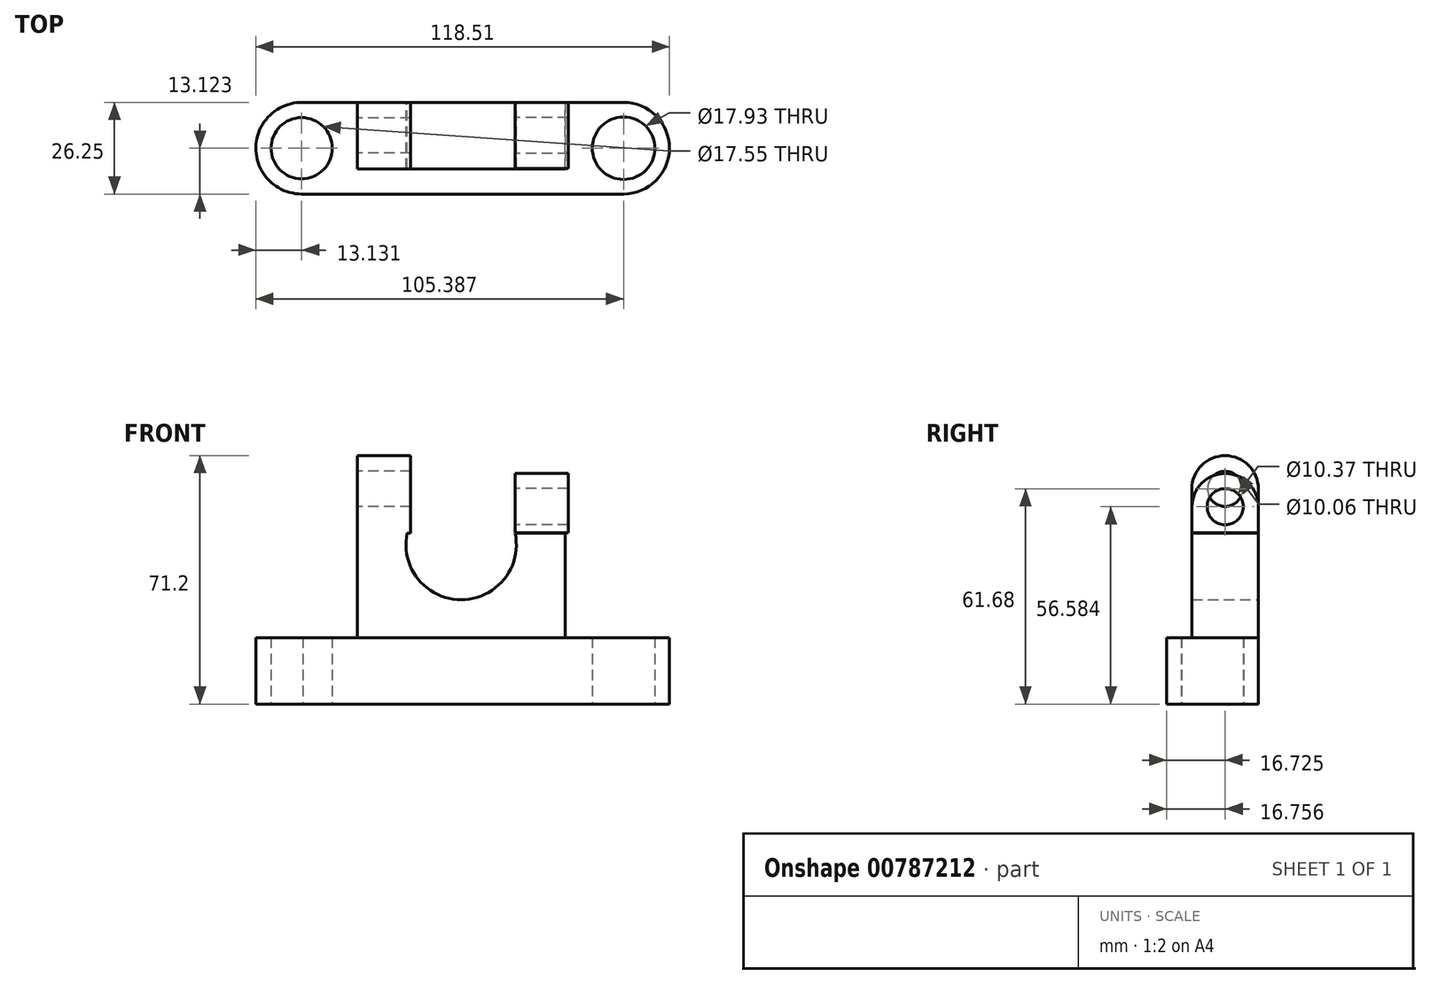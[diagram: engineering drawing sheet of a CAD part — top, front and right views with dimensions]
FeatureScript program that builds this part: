
annotation { "Feature Type Name" : "Feature", "Feature Type Description" : "" }
export const myFeature = defineFeature(function(context is Context, id is Id, definition is map)
    precondition{}
    {
        {
            var Q0;
            Q0=qCreatedBy(makeId("Top.planeOp"),FACE);
            var sketch = newSketch(context, id + "F0", { "sketchPlane" : qUnion([Q0])});
            skLineSegment(sketch, "E0.bottom", {"start": v(-60.85, 0) * mm, "end": v(31.08, 0) * mm});
            skLineSegment(sketch, "E1.bottom", {"start": v(-61.18, -26.25) * mm, "end": v(31.08, -26.25) * mm});
            skLineSegment(sketch, "E1.top", {"start": v(-61.18, 0) * mm, "end": v(31.08, 0) * mm});
            skCircle(sketch, "E2", {"center": v(-61.18, -13.13) * mm, "radius": 8.78 * mm});
            skCircle(sketch, "E3", {"center": v(31.08, -13.13) * mm, "radius": 8.96 * mm});
            skArc(sketch, "E4", {"start": v(-60.85, 0) * mm, "mid": v(-74.3, -12.96) * mm, "end": v(-61.18, -26.25) * mm});
            skArc(sketch, "E5", {"start": v(31.08, -26.25) * mm, "mid": v(44.2, -13.13) * mm, "end": v(31.08, 0) * mm});
            skSolve(sketch);
        }
        {
            var Q0;
            {var subQ4=sQuery(id+"F0.wireOp",EDGE,"E0.bottom");Q0=makeQuery(id+"F0.imprint","IMPRINT",FACE,{"disambiguationData":[TD([[makeQuery(id+"F0.imprint","IMPRINT",EDGE,{"derivedFrom":subQ4}),-1.0]])]});}
            var Q1;
            {var subQ1=sQuery(id+"F0.wireOp",EDGE,"E1.bottom");Q1=makeQuery(id+"F0.imprint","IMPRINT",FACE,{"disambiguationData":[TD([[makeQuery(id+"F0.imprint","IMPRINT",EDGE,{"derivedFrom":subQ1}),1.0]])]});}
            extrude(context, id + "F1", {"entities" : qUnion([Q0, Q1]), "depth" : 19.05 * mm, "offsetDistance" : 25.4 * mm});
        }
        {
            var Q0;
            Q0=qCreatedBy(makeId("Front.planeOp"),FACE);
            var sketch = newSketch(context, id + "F2", { "sketchPlane" : qUnion([Q0])});
            skLineSegment(sketch, "E6.bottom", {"start": v(-45.19, 19.02) * mm, "end": v(14.34, 19.02) * mm});
            skLineSegment(sketch, "E6.left", {"start": v(-45.19, 19.02) * mm, "end": v(-45.19, 48.98) * mm});
            skLineSegment(sketch, "E6.right", {"start": v(14.34, 19.02) * mm, "end": v(14.34, 48.98) * mm});
            skLineSegment(sketch, "E7", {"start": v(-30.97, 48.98) * mm, "end": v(-45.19, 48.98) * mm});
            skLineSegment(sketch, "E8", {"start": v(0, 48.98) * mm, "end": v(14.34, 48.98) * mm});
            skArc(sketch, "E9", {"start": v(-30.97, 48.98) * mm, "mid": v(-15.48, 29.9) * mm, "end": v(0, 48.98) * mm});
            skSolve(sketch);
        }
        {
            var Q0;
            Q0 = qSketchRegion(id + "F2", true);
            extrude(context, id + "F3", {"entities" : qUnion([Q0]), "operationType" : NewBodyOperationType.ADD, "depth" : 19.05 * mm, "offsetDistance" : 25.4 * mm});
        }
        {
            var Q0;
            Q0=qCreatedBy(makeId("Right.planeOp"),FACE);
            var sketch = newSketch(context, id + "F4", { "sketchPlane" : qUnion([Q0])});
            skLineSegment(sketch, "E10", {"start": v(0, 49.11) * mm, "end": v(0, 56.58) * mm});
            skLineSegment(sketch, "E11", {"start": v(-18.99, 49.11) * mm, "end": v(-18.99, 56.58) * mm});
            skArc(sketch, "E12", {"start": v(0, 56.58) * mm, "mid": v(-9.5, 66.08) * mm, "end": v(-18.99, 56.58) * mm});
            skCircle(sketch, "E13", {"center": v(-9.5, 56.58) * mm, "radius": 5.18 * mm});
            skLineSegment(sketch, "E14", {"start": v(0, 49.11) * mm, "end": v(-18.99, 49.11) * mm});
            skSolve(sketch);
        }
        {
            var Q0;
            Q0=makeQuery(id+"F4.imprint","IMPRINT",FACE,{"disambiguationData":[TD([[makeQuery(id+"F4.imprint","IMPRINT",EDGE,{"derivedFrom":sQuery(id+"F4.wireOp",EDGE,"E10")}),1.0]])]});
            extrude(context, id + "F5", {"entities" : qUnion([Q0]), "depth" : 15.24 * mm, "offsetDistance" : 25.4 * mm});
        }
        {
            var Q0;
            Q0=makeQuery(id+"F3.opExtrude","SWEPT_FACE",FACE,{"disambiguationData":[OSD([sQuery(id+"F2.wireOp",EDGE,"E6.left")])]});
            var sketch = newSketch(context, id + "F6", { "sketchPlane" : qUnion([Q0])});
            skArc(sketch, "E15", {"start": v(19.05, 61.68) * mm, "mid": v(9.52, 71.2) * mm, "end": v(0, 61.68) * mm});
            skCircle(sketch, "E16", {"center": v(9.52, 61.68) * mm, "radius": 5.03 * mm});
            skLineSegment(sketch, "E17", {"start": v(14.55, 61.68) * mm, "end": v(19.05, 61.68) * mm});
            skLineSegment(sketch, "E18", {"start": v(4.5, 61.68) * mm, "end": v(0, 61.68) * mm});
            skLineSegment(sketch, "E19", {"start": v(0, 61.68) * mm, "end": v(0, 48.98) * mm});
            skLineSegment(sketch, "E20", {"start": v(19.05, 61.68) * mm, "end": v(19.05, 48.98) * mm});
            skSolve(sketch);
        }
        {
            var Q0;
            Q0=makeQuery(id+"F6.imprint","IMPRINT",FACE,{"disambiguationData":[TD([[makeQuery(id+"F6.imprint","IMPRINT",EDGE,{"derivedFrom":sQuery(id+"F6.wireOp",EDGE,"E15")}),1.0]])]});
            var Q1;
            {var subQ1=sQuery(id+"F6.wireOp",EDGE,"E17");Q1=makeQuery(id+"F6.imprint","IMPRINT",FACE,{"disambiguationData":[TD([[makeQuery(id+"F6.imprint","IMPRINT",EDGE,{"derivedFrom":subQ1}),-1.0]])]});}
            extrude(context, id + "F7", {"entities" : qUnion([Q0, Q1]), "operationType" : NewBodyOperationType.ADD, "depth" : -15.24 * mm, "offsetDistance" : 25.4 * mm});
        }
    });
